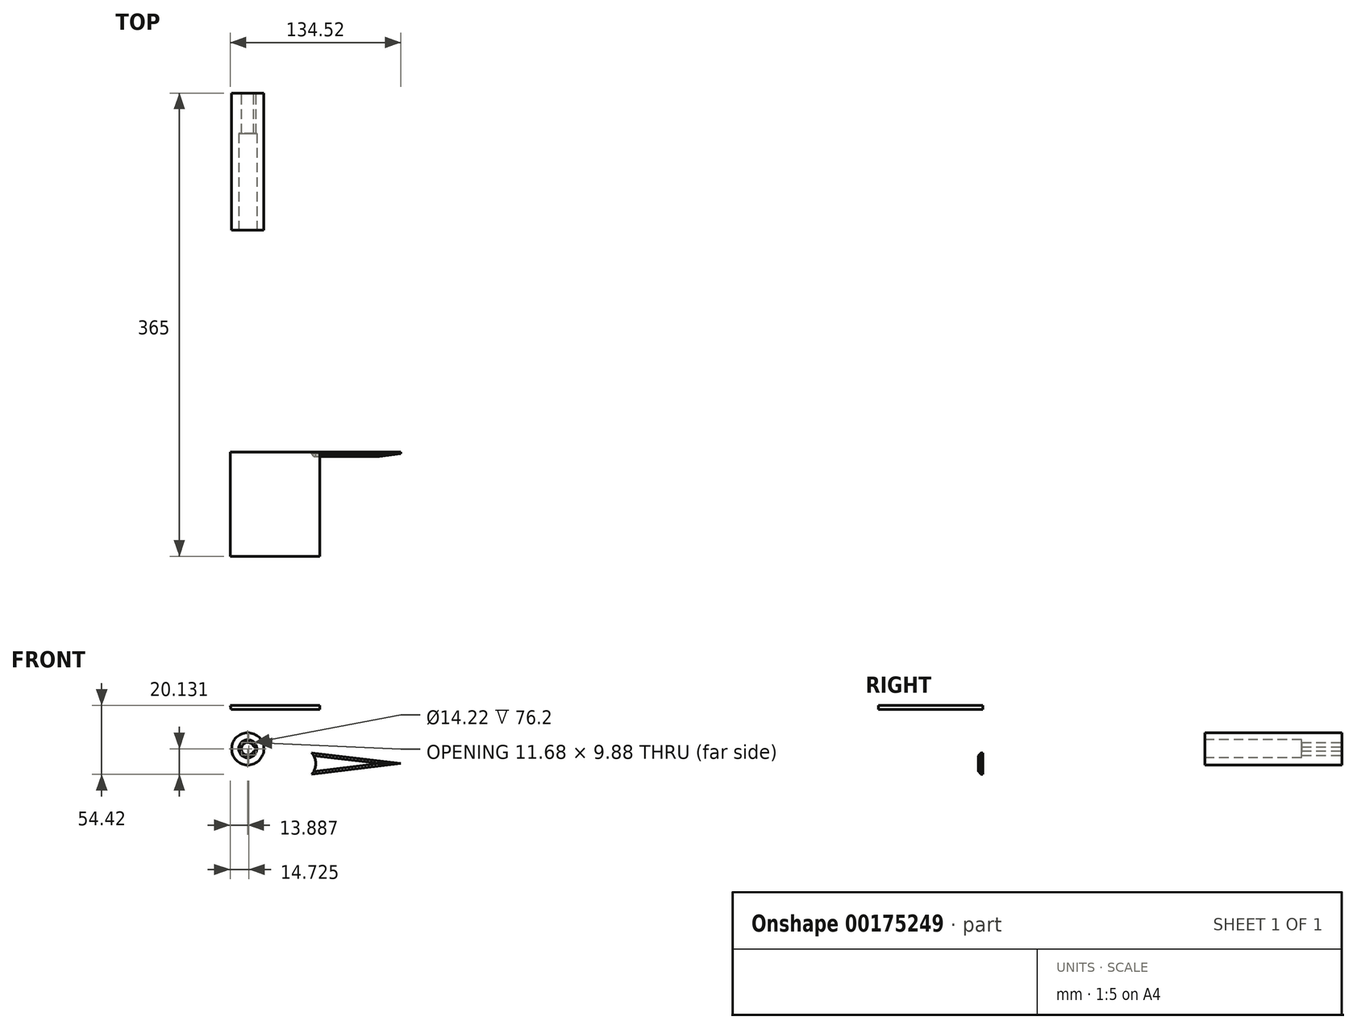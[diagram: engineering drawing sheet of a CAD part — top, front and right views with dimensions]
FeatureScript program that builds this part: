
annotation { "Feature Type Name" : "Feature", "Feature Type Description" : "" }
export const myFeature = defineFeature(function(context is Context, id is Id, definition is map)
    precondition{}
    {
        {
            var Q0;
            Q0=qCreatedBy(makeId("Front.planeOp"),FACE);
            var sketch = newSketch(context, id + "F0", { "sketchPlane" : qUnion([Q0])});
            skLineSegment(sketch, "E0", {"start": v(-53.88, 42.6) * mm, "end": v(15.85, 42.6) * mm});
            skLineSegment(sketch, "E1", {"start": v(15.85, 42.6) * mm, "end": v(15.85, 45.91) * mm});
            skLineSegment(sketch, "E2", {"start": v(15.85, 45.91) * mm, "end": v(-54.76, 45.91) * mm});
            skLineSegment(sketch, "E3", {"start": v(-54.76, 45.91) * mm, "end": v(-53.88, 42.6) * mm});
            skPoint(sketch, "E4.orphan", {"position": v(-54.76, 42.6) * mm});
            skSolve(sketch);
        }
        {
            var Q0;
            Q0=makeQuery(id+"F0.imprint","IMPRINT",FACE,{"disambiguationData":[TD([[makeQuery(id+"F0.imprint","IMPRINT",EDGE,{"derivedFrom":sQuery(id+"F0.wireOp",EDGE,"E0")}),1.0]])]});
            extrude(context, id + "F1", {"entities" : qUnion([Q0]), "depth" : 82.04 * mm});
        }
        {
            var Q0;
            Q0=qCreatedBy(makeId("Front.planeOp"),FACE);
            var sketch = newSketch(context, id + "F2", { "sketchPlane" : qUnion([Q0])});
            skCircle(sketch, "E5", {"center": v(-40.87, 11.62) * mm, "radius": 12.7 * mm});
            skArc(sketch, "E6", {"start": v(-36.12, 13.2) * mm, "mid": v(-45.88, 11.62) * mm, "end": v(-36.12, 10.05) * mm});
            skLineSegment(sketch, "E7", {"start": v(-34.2, 11.62) * mm, "end": v(-34.2, 13.2) * mm});
            skLineSegment(sketch, "E8", {"start": v(-34.2, 11.62) * mm, "end": v(-34.2, 10.05) * mm});
            skLineSegment(sketch, "E9.trimOffspring", {"start": v(-36.12, 13.2) * mm, "end": v(-34.2, 13.2) * mm});
            skLineSegment(sketch, "E10.trimOffspring", {"start": v(-36.12, 10.05) * mm, "end": v(-34.2, 10.05) * mm});
            skSolve(sketch);
        }
        {
            var Q0;
            Q0=makeQuery(id+"F2.imprint","IMPRINT",FACE,{"disambiguationData":[TD([[makeQuery(id+"F2.imprint","IMPRINT",EDGE,{"derivedFrom":sQuery(id+"F2.wireOp",EDGE,"E5")}),1.0]])]});
            extrude(context, id + "F3", {"entities" : qUnion([Q0]), "depth" : 25.4 * mm});
        }
        {
            var Q0;
            Q0=qCreatedBy(makeId("Front.planeOp"),FACE);
            var sketch = newSketch(context, id + "F4", { "sketchPlane" : qUnion([Q0])});
            skArc(sketch, "E11", {"start": v(9.43, -8.5) * mm, "mid": v(12.7, 0) * mm, "end": v(9.43, 8.5) * mm});
            skLineSegment(sketch, "E12", {"start": v(79.76, 0) * mm, "end": v(9.43, 8.5) * mm});
            skLineSegment(sketch, "E13", {"start": v(9.43, -8.5) * mm, "end": v(79.76, 0) * mm});
            skSolve(sketch);
        }
        {
            var Q0;
            Q0=makeQuery(id+"F4.imprint","IMPRINT",FACE,{"disambiguationData":[TD([[makeQuery(id+"F4.imprint","IMPRINT",EDGE,{"derivedFrom":sQuery(id+"F4.wireOp",EDGE,"E11")}),-1.0]])]});
            extrude(context, id + "F5", {"entities" : qUnion([Q0]), "depth" : 3.3 * mm});
        }
        {
            var Q0;
            Q0=makeQuery(id+"F5.opExtrude","CAP_EDGE",EDGE,{"disambiguationData":[OSD([sQuery(id+"F4.wireOp",EDGE,"E12")])],"isStart":false});
            var Q1;
            Q1=makeQuery(id+"F5.opExtrude","CAP_EDGE",EDGE,{"disambiguationData":[OSD([sQuery(id+"F4.wireOp",EDGE,"E13")])],"isStart":false});
            chamfer(context, id + "F6", {"entities" : qUnion([Q0, Q1]), "width" : 2.03 * mm, "tangentPropagation" : true});
        }
        {
            var Q0;
            Q0=makeQuery(id+"F3.opExtrude","CAP_FACE",FACE,{"disambiguationData":[OSD([sQuery(id+"F2.wireOp",EDGE,"E5"),sQuery(id+"F2.wireOp",EDGE,"E6"),sQuery(id+"F2.wireOp",EDGE,"E7"),sQuery(id+"F2.wireOp",EDGE,"E8"),sQuery(id+"F2.wireOp",EDGE,"E9.trimOffspring"),sQuery(id+"F2.wireOp",EDGE,"E10.trimOffspring")])],"isStart":true});
            extrude(context, id + "F7", {"entities" : qUnion([Q0]), "operationType" : NewBodyOperationType.ADD, "depth" : 6.35 * mm});
        }
        {
            var Q0;
            Q0=makeQuery(id+"F3.opExtrude","SWEPT_BODY",BODY,{"disambiguationData":[OSD([sQuery(id+"F2.wireOp",EDGE,"E5"),sQuery(id+"F2.wireOp",EDGE,"E6"),sQuery(id+"F2.wireOp",EDGE,"E7"),sQuery(id+"F2.wireOp",EDGE,"E8"),sQuery(id+"F2.wireOp",EDGE,"E9.trimOffspring"),sQuery(id+"F2.wireOp",EDGE,"E10.trimOffspring")])]});
            transform(context, id + "F8", {"entities" : qUnion([Q0]), "transformType" : TransformType.TRANSLATION_3D, "dx" : 0 * mm, "dy" : 276.6 * mm, "dz" : 0 * mm, "makeCopy" : false});
        }
        {
            var Q0;
            Q0=makeQuery(id+"F3.opExtrude","CAP_FACE",FACE,{"disambiguationData":[OSD([sQuery(id+"F2.wireOp",EDGE,"E5"),sQuery(id+"F2.wireOp",EDGE,"E6"),sQuery(id+"F2.wireOp",EDGE,"E7"),sQuery(id+"F2.wireOp",EDGE,"E8"),sQuery(id+"F2.wireOp",EDGE,"E9.trimOffspring"),sQuery(id+"F2.wireOp",EDGE,"E10.trimOffspring")])],"isStart":false});
            var sketch = newSketch(context, id + "F9", { "sketchPlane" : qUnion([Q0])});
            skCircle(sketch, "E14", {"center": v(-40.87, 11.62) * mm, "radius": 12.7 * mm});
            skSolve(sketch);
        }
        {
            var Q0;
            Q0 = qSketchRegion(id + "F9", true);
            extrude(context, id + "F10", {"entities" : qUnion([Q0]), "operationType" : NewBodyOperationType.ADD, "depth" : 76.2 * mm});
        }
        {
            var Q0;
            Q0=makeQuery(id+"F10.opExtrude","CAP_FACE",FACE,{"disambiguationData":[OSD([sQuery(id+"F9.wireOp",EDGE,"E14")])],"isStart":false});
            var sketch = newSketch(context, id + "F11", { "sketchPlane" : qUnion([Q0])});
            skCircle(sketch, "E15", {"center": v(-40.87, 11.62) * mm, "radius": 7.11 * mm});
            skSolve(sketch);
        }
        {
            var Q0;
            Q0=makeQuery(id+"F11.imprint","IMPRINT",FACE,{"disambiguationData":[TD([[makeQuery(id+"F11.imprint","IMPRINT",EDGE,{"derivedFrom":sQuery(id+"F11.wireOp",EDGE,"E15")}),1.0]])]});
            extrude(context, id + "F12", {"entities" : qUnion([Q0]), "operationType" : NewBodyOperationType.REMOVE, "oppositeDirection" : true, "depth" : 76.2 * mm});
        }
        {
            var Q0;
            {var subQ0=sQuery(id+"F2.wireOp",EDGE,"E8");var subQ1=sQuery(id+"F2.wireOp",EDGE,"E7");Q0=makeQuery(id+"F7.boolean.opBoolean","MERGE",FACE,{"derivedFrom":[makeQuery(id+"F3.opExtrude","SWEPT_FACE",FACE,{"disambiguationData":[OSD([subQ1,subQ0])]}),makeQuery(id+"F7.opExtrude","SWEPT_FACE",FACE,{"disambiguationData":[OSD([subQ1,subQ0])]})]});}
            cPlane(context, id + "F13", {"entities" : qUnion([Q0]), "cplaneType" : CPlaneType.OFFSET, "offset" : 25.4 * mm, "oppositeDirection" : true, "width" : 152.4 * mm, "height" : 152.4 * mm});
        }
    });
